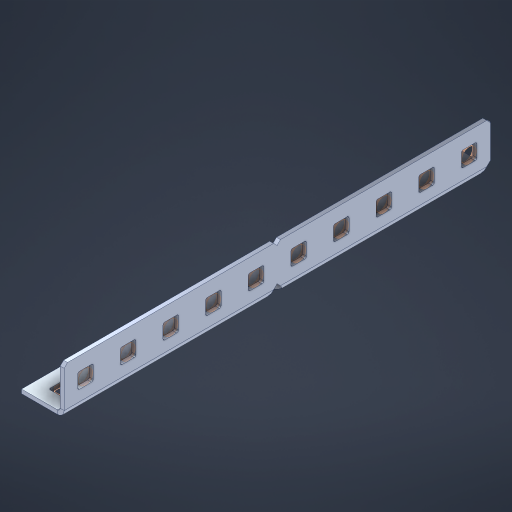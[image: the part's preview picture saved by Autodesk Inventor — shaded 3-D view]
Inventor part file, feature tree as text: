
AUTODESK INVENTOR PART (.ipt)
format: ipt  version: 2023 (Build 270158000, 158)  size: 555,008 bytes
history: native  units: in
note: dims shown in document units (in); Inventor stores cm internally (conversion verified against a paired STEP export)
features: other x25, extrude x19, sheet_metal_op x10, sketch x8, mirror x1, pattern_linear x1, chamfer x1
ambient origin geometry x8: Origin, YZ Plane, XZ Plane, XY Plane, X Axis, Y Axis, Z Axis, Center Point
bodies: Solid1 (feature_tree), Body (feature_tree)
feature tree (65):
  other  "Flange Pattern Plane"
  sheet_metal_op  "Flange Pattern"
  sheet_metal_op  "Body Pattern"
  other  "Arc Length"
  mirror  "Notch Mirror"
  pattern_linear  "Notch Pattern"  Spacing1=0.1875in  [1 undecoded]
  chamfer  "End Chamfer"
  extrude  "Half Cut"  Depth=0.0469in
  sketch  "Sketch1"  dims[d0=2.5in]
  other  "Plate1"
  sketch  "Sketch2"  dims[d1=5.0in]
  other  "Plate2"
  sheet_metal_op  "Bend1"
  sheet_metal_op  "Corner1"
  sketch  "Sketch3"  dims[d2=0.0469in]
  other  "Flange Pattern Sketch"
  sketch  "Sketch7"  dims[d3=0.0469in]
  other  "Srf1"
  other  "Srf2"
  sketch  "Sketch8"  dims[d4=0.0234in]
  sketch  "Sketch9"  dims[d5=0.0938in]
  other  "Srf91"
  sheet_metal_op  "Body Pattern Sketch"
  other  "Srf92"
  sketch  "Sketch13"  dims[d6=0.0469in]
  sketch  "Sketch14"  dims[d7=0.5in d8=90.0deg d9=0.0312in d10=0.1875in d11=0.0469in d12=0.0469in d16=0.182in d17=0.02in d18=0.0469in d19=0.0in d20=0.25in d21=0.25in d46=0.172in d47=1.0in d48=0.0in d49=0.182in d50=0.02in d51=0.25in d52=0.25in d53=0.0469in d54=0.0in d55=0.172in d56=1.0in d57=0.0in d60=3.937in d62=0.5in d63=0.3937in d65=0.5in d85=0.1227in d86=0.1659in d88=0.04in d89=0.0469in d90=0.0in d91=0.04in d92=0.0491in d95=2.5in d96=0.04in d97=0.25in d98=45.0deg d101=0.0in d102=2.497in d131=0.5in d132=3.937in d134=0.5in d139=0.5in]
  other  "Srf856"
  other  "Srf1310"
  other  "Srf1311"
  other  "Srf1312"
  other  "Srf1376"
  other  "Srf1377"
  other  "Srf1728"
  other  "Srf1755"
  other  "Srf1878"
  other  "Srf1879"
  other  "Srf1880"
  other  "Srf1881"
  other  "Srf1942"
  other  "Srf1943"
  other  "Srf1944"
  other  "Srf1945"
  sheet_metal_op  "Flange Stamp"
  sheet_metal_op  "Flange Circle"
  sheet_metal_op  "Body Stamp"
  sheet_metal_op  "Body Circle"
  sheet_metal_op  "Notch"
  extrude  "ExtrusionSrf2"  Depth=0.0469in
  extrude  "ExtrusionSrf92"  Depth=0.5in
  extrude  "ExtrusionSrf856"  Depth=0.02in
  extrude  "ExtrusionSrf1310"  Depth=0.0469in
  extrude  "ExtrusionSrf1311"  TaperAngle=0.0deg  [1 undecoded]
  extrude  "ExtrusionSrf1312"  Depth=0.5in
  extrude  "ExtrusionSrf1376"  Depth=0.5in
  extrude  "ExtrusionSrf1377"  Depth=0.5in
  extrude  "ExtrusionSrf1728"  Depth=0.5in TaperAngle=0.0deg
  extrude  "ExtrusionSrf1755"  Depth=0.5in
  extrude  "ExtrusionSrf1878"  Depth=0.02in
  extrude  "ExtrusionSrf1879"  Depth=0.5in
  extrude  "ExtrusionSrf1880"  Depth=0.5in
  extrude  "ExtrusionSrf1881"  Depth=0.0469in
  extrude  "ExtrusionSrf1942"  TaperAngle=0.0deg  [1 undecoded]
  extrude  "ExtrusionSrf1943"  Depth=0.5in
  extrude  "ExtrusionSrf1944"  Depth=0.5in TaperAngle=0.0deg
  extrude  "ExtrusionSrf1945"  Depth=0.5in
note: 3 required parameter values undecoded (feature->parameter linkage not recoverable at this tier; creation-order binding heuristic only, values carry confidence <= 0.55)
